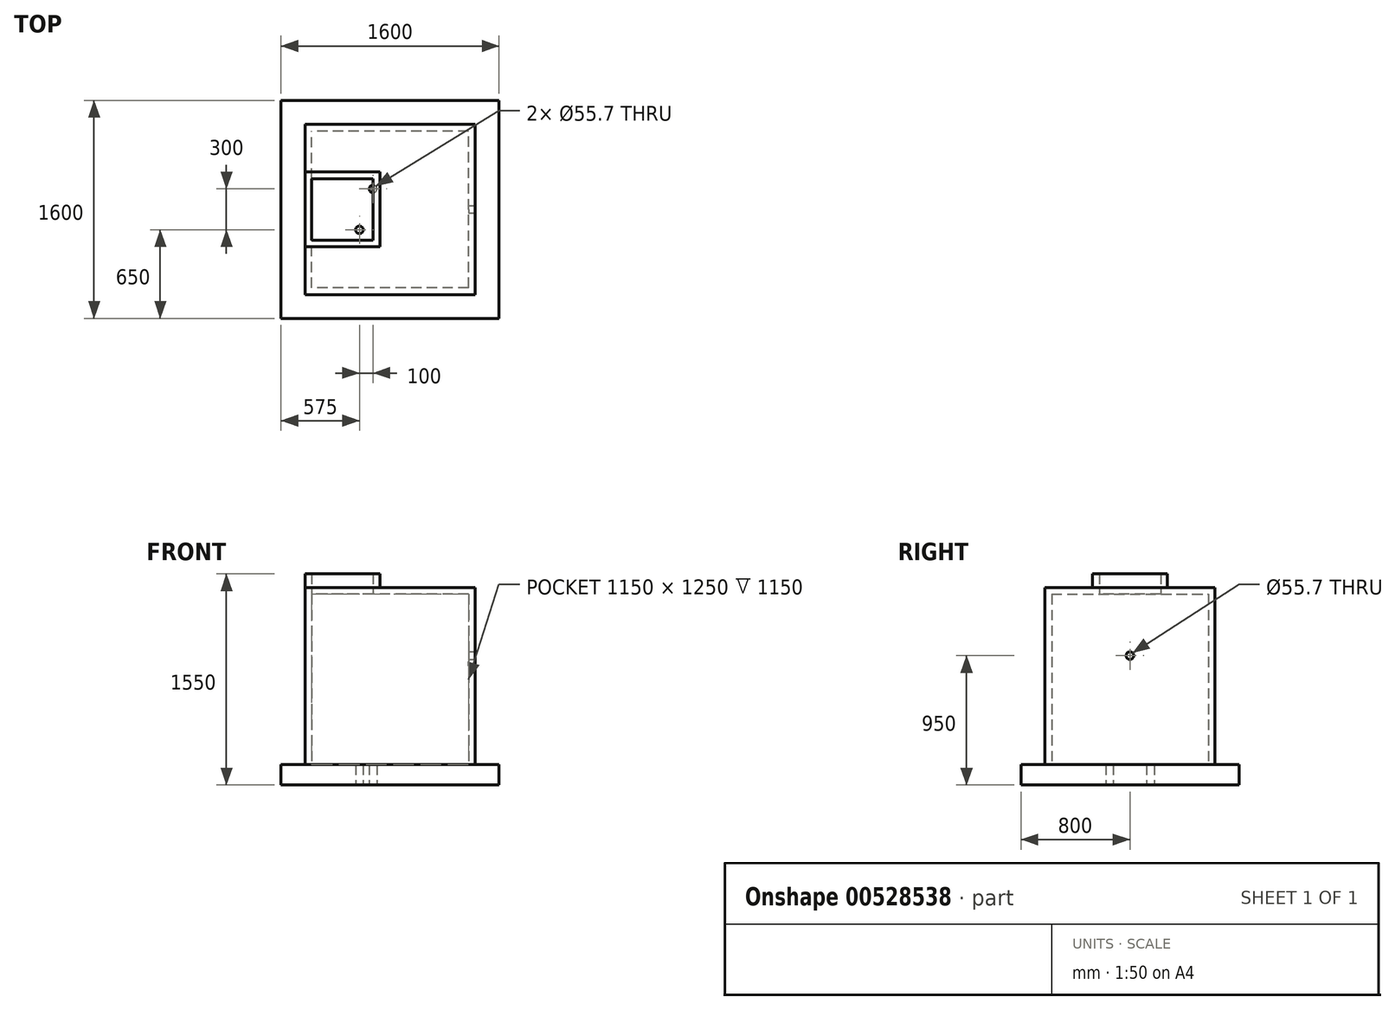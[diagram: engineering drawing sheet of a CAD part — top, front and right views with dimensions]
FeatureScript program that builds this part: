
annotation { "Feature Type Name" : "Feature", "Feature Type Description" : "" }
export const myFeature = defineFeature(function(context is Context, id is Id, definition is map)
    precondition{}
    {
        {
            var Q0;
            Q0=qCreatedBy(makeId("Top.planeOp"),FACE);
            var sketch = newSketch(context, id + "F0", { "sketchPlane" : qUnion([Q0])});
            skLineSegment(sketch, "E0.bottom", {"start": v(800, -800) * mm, "end": v(-800, -800) * mm});
            skLineSegment(sketch, "E0.top", {"start": v(800, 800) * mm, "end": v(-800, 800) * mm});
            skLineSegment(sketch, "E0.left", {"start": v(800, -800) * mm, "end": v(800, 800) * mm});
            skLineSegment(sketch, "E0.right", {"start": v(-800, -800) * mm, "end": v(-800, 800) * mm});
            skPoint(sketch, "E0.middle", {"position": v(0, 0) * mm});
            skSolve(sketch);
        }
        {
            var Q0;
            Q0=qCreatedBy(makeId("Top.planeOp"),FACE);
            var sketch = newSketch(context, id + "F1", { "sketchPlane" : qUnion([Q0])});
            skLineSegment(sketch, "E1.bottom", {"start": v(625, -625) * mm, "end": v(-625, -625) * mm});
            skLineSegment(sketch, "E1.top", {"start": v(625, 625) * mm, "end": v(-625, 625) * mm});
            skLineSegment(sketch, "E1.left", {"start": v(625, -625) * mm, "end": v(625, 625) * mm});
            skLineSegment(sketch, "E1.right", {"start": v(-625, -625) * mm, "end": v(-625, 625) * mm});
            skPoint(sketch, "E1.middle", {"position": v(0, 0) * mm});
            skLineSegment(sketch, "E2.bottom", {"start": v(575, -575) * mm, "end": v(-575, -575) * mm});
            skLineSegment(sketch, "E2.top", {"start": v(575, 575) * mm, "end": v(-575, 575) * mm});
            skLineSegment(sketch, "E2.left", {"start": v(-575, -575) * mm, "end": v(-575, 575) * mm});
            skLineSegment(sketch, "E2.right", {"start": v(575, -575) * mm, "end": v(575, 575) * mm});
            skSolve(sketch);
        }
        {
            var Q0;
            Q0=makeQuery(id+"F0.imprint","IMPRINT",FACE,{"disambiguationData":[TD([[makeQuery(id+"F0.imprint","IMPRINT",EDGE,{"derivedFrom":sQuery(id+"F0.wireOp",EDGE,"E0.bottom")}),-1.0]])]});
            extrude(context, id + "F2", {"entities" : qUnion([Q0]), "oppositeDirection" : true, "depth" : 150 * mm, "offsetDistance" : 25 * mm});
        }
        {
            var Q0;
            Q0=makeQuery(id+"F1.imprint","IMPRINT",FACE,{"disambiguationData":[TD([[makeQuery(id+"F1.imprint","IMPRINT",EDGE,{"derivedFrom":sQuery(id+"F1.wireOp",EDGE,"E1.bottom")}),-1.0]])]});
            extrude(context, id + "F3", {"entities" : qUnion([Q0]), "operationType" : NewBodyOperationType.ADD, "depth" : 1250 * mm, "offsetDistance" : 25 * mm});
        }
        {
            var Q0;
            Q0=makeQuery(id+"F3.opExtrude","CAP_FACE",FACE,{"disambiguationData":[OSD([sQuery(id+"F1.wireOp",EDGE,"E1.bottom"),sQuery(id+"F1.wireOp",EDGE,"E1.top"),sQuery(id+"F1.wireOp",EDGE,"E1.left"),sQuery(id+"F1.wireOp",EDGE,"E1.right"),sQuery(id+"F1.wireOp",EDGE,"E2.bottom"),sQuery(id+"F1.wireOp",EDGE,"E2.top"),sQuery(id+"F1.wireOp",EDGE,"E2.left"),sQuery(id+"F1.wireOp",EDGE,"E2.right")])],"isStart":false});
            var sketch = newSketch(context, id + "F4", { "sketchPlane" : qUnion([Q0])});
            skLineSegment(sketch, "E3.0", {"start": v(625, -625) * mm, "end": v(625, 625) * mm});
            skLineSegment(sketch, "E4.0", {"start": v(625, 625) * mm, "end": v(-625, 625) * mm});
            skLineSegment(sketch, "E5.0", {"start": v(625, -625) * mm, "end": v(-625, -625) * mm});
            skLineSegment(sketch, "E6.0.0", {"start": v(-625, 625) * mm, "end": v(-625, -625) * mm});
            skLineSegment(sketch, "E6.0.2", {"start": v(-625, -625) * mm, "end": v(-625, 625) * mm});
            skLineSegment(sketch, "E7.bottom", {"start": v(-125, 225) * mm, "end": v(-575, 225) * mm});
            skLineSegment(sketch, "E7.top", {"start": v(-125, -225) * mm, "end": v(-575, -225) * mm});
            skLineSegment(sketch, "E7.left", {"start": v(-125, 225) * mm, "end": v(-125, -225) * mm});
            skLineSegment(sketch, "E7.right", {"start": v(-575, 225) * mm, "end": v(-575, -225) * mm});
            skSolve(sketch);
        }
        {
            var Q0;
            Q0=qSketchRegion(id+"F4",true);
            extrude(context, id + "F5", {"entities" : qUnion([Q0]), "operationType" : NewBodyOperationType.ADD, "depth" : 50 * mm, "offsetDistance" : 25 * mm});
        }
        {
            var Q0;
            Q0=makeQuery(id+"F5.opExtrude","CAP_FACE",FACE,{"disambiguationData":[OSD([sQuery(id+"F4.wireOp",EDGE,"E3.0"),sQuery(id+"F4.wireOp",EDGE,"E4.0"),sQuery(id+"F4.wireOp",EDGE,"E5.0"),sQuery(id+"F4.wireOp",EDGE,"E6.0.2"),sQuery(id+"F4.wireOp",EDGE,"E7.bottom"),sQuery(id+"F4.wireOp",EDGE,"E7.top"),sQuery(id+"F4.wireOp",EDGE,"E7.left"),sQuery(id+"F4.wireOp",EDGE,"E7.right")])],"isStart":false});
            var sketch = newSketch(context, id + "F6", { "sketchPlane" : qUnion([Q0])});
            skLineSegment(sketch, "E8.bottom", {"start": v(-625, 275) * mm, "end": v(-75, 275) * mm});
            skLineSegment(sketch, "E8.top", {"start": v(-625, -275) * mm, "end": v(-75, -275) * mm});
            skLineSegment(sketch, "E8.left", {"start": v(-625, 275) * mm, "end": v(-625, -275) * mm});
            skLineSegment(sketch, "E8.right", {"start": v(-75, 275) * mm, "end": v(-75, -275) * mm});
            skLineSegment(sketch, "E9.0", {"start": v(-125, 225) * mm, "end": v(-125, -225) * mm});
            skLineSegment(sketch, "E10.0", {"start": v(-125, -225) * mm, "end": v(-575, -225) * mm});
            skLineSegment(sketch, "E11.0", {"start": v(-575, -225) * mm, "end": v(-575, 225) * mm});
            skLineSegment(sketch, "E12.0", {"start": v(-125, 225) * mm, "end": v(-575, 225) * mm});
            skSolve(sketch);
        }
        {
            var Q0;
            Q0=makeQuery(id+"F6.imprint","IMPRINT",FACE,{"disambiguationData":[TD([[makeQuery(id+"F6.imprint","IMPRINT",EDGE,{"derivedFrom":sQuery(id+"F6.wireOp",EDGE,"E8.bottom")}),-1.0]])]});
            extrude(context, id + "F7", {"entities" : qUnion([Q0]), "operationType" : NewBodyOperationType.ADD, "depth" : 100 * mm, "offsetDistance" : 25 * mm});
        }
        {
            var Q0;
            Q0=makeQuery(id+"F5.boolean.opBoolean","MERGE",FACE,{"derivedFrom":[makeQuery(id+"F3.opExtrude","SWEPT_FACE",FACE,{"disambiguationData":[OSD([sQuery(id+"F1.wireOp",EDGE,"E1.left")])]}),makeQuery(id+"F5.opExtrude","SWEPT_FACE",FACE,{"disambiguationData":[OSD([sQuery(id+"F4.wireOp",EDGE,"E3.0")])]})]});
            var sketch = newSketch(context, id + "F8", { "sketchPlane" : qUnion([Q0])});
            skCircle(sketch, "E13", {"center": v(0, 800) * mm, "radius": 27.85 * mm});
            skSolve(sketch);
        }
        {
            var Q0;
            Q0=makeQuery(id+"F8.imprint","IMPRINT",FACE,{"disambiguationData":[TD([[makeQuery(id+"F8.imprint","IMPRINT",EDGE,{"derivedFrom":sQuery(id+"F8.wireOp",EDGE,"E13")}),1.0]])]});
            extrude(context, id + "F9", {"entities" : qUnion([Q0]), "operationType" : NewBodyOperationType.REMOVE, "oppositeDirection" : true, "depth" : 100 * mm, "offsetDistance" : 25 * mm});
        }
        {
            var Q0;
            Q0=makeQuery(id+"F2.opExtrude","CAP_FACE",FACE,{"disambiguationData":[OSD([sQuery(id+"F0.wireOp",EDGE,"E0.bottom"),sQuery(id+"F0.wireOp",EDGE,"E0.top"),sQuery(id+"F0.wireOp",EDGE,"E0.left"),sQuery(id+"F0.wireOp",EDGE,"E0.right")])],"isStart":false});
            var sketch = newSketch(context, id + "F10", { "sketchPlane" : qUnion([Q0])});
            skCircle(sketch, "E14", {"center": v(-125, -150) * mm, "radius": 27.85 * mm});
            skCircle(sketch, "E15", {"center": v(-225, 150) * mm, "radius": 27.85 * mm});
            skSolve(sketch);
        }
        {
            var Q0;
            Q0=qSketchRegion(id+"F10",true);
            extrude(context, id + "F11", {"entities" : qUnion([Q0]), "operationType" : NewBodyOperationType.REMOVE, "oppositeDirection" : true, "depth" : 200 * mm, "offsetDistance" : 25 * mm});
        }
    });
